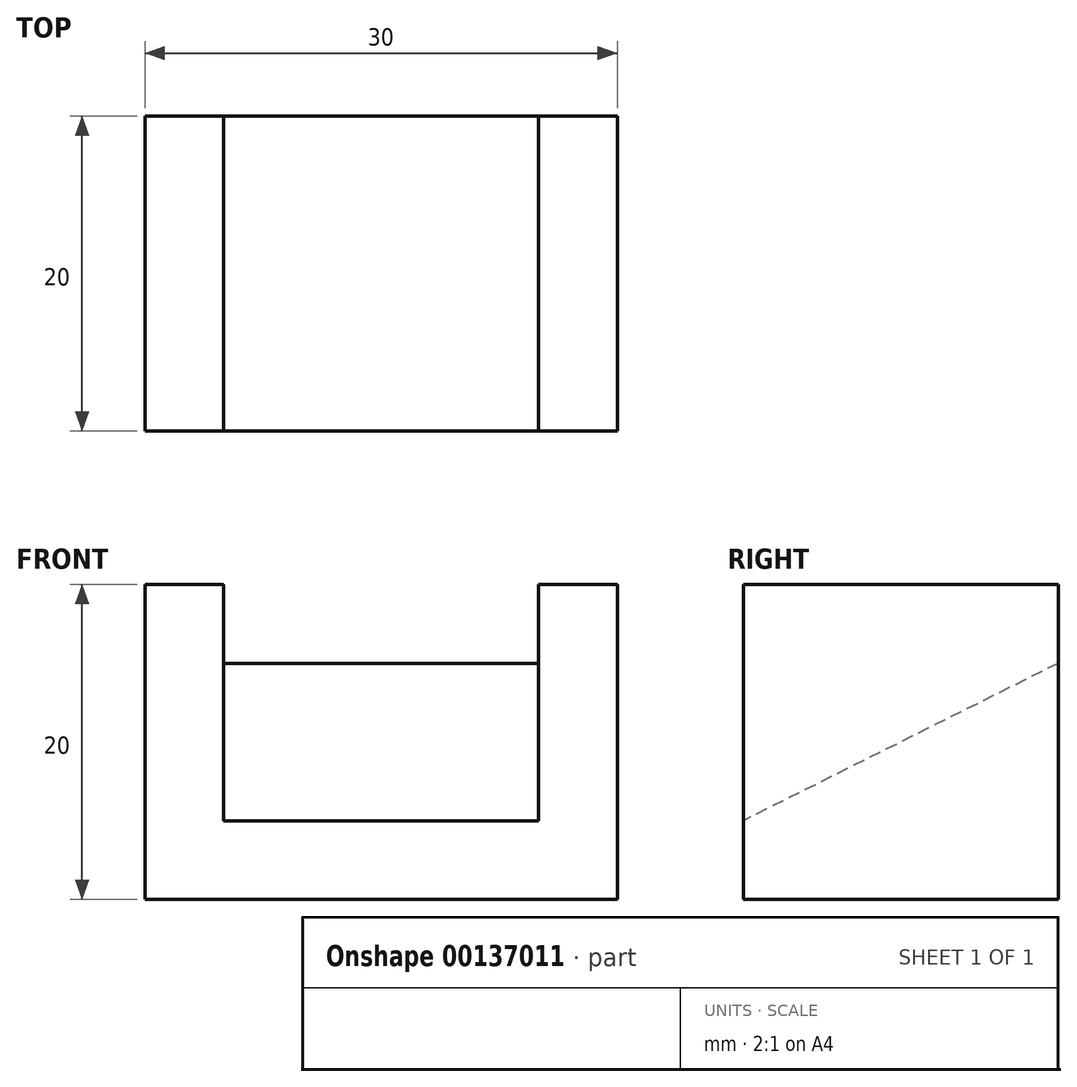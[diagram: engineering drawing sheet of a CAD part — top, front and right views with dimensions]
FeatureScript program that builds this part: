
annotation { "Feature Type Name" : "Feature", "Feature Type Description" : "" }
export const myFeature = defineFeature(function(context is Context, id is Id, definition is map)
    precondition{}
    {
        {
            var Q0;
            Q0=qCreatedBy(makeId("Front.planeOp"),FACE);
            var sketch = newSketch(context, id + "F0", { "sketchPlane" : qUnion([Q0])});
            skLineSegment(sketch, "E0", {"start": v(-10, 15) * mm, "end": v(-10, 0) * mm});
            skLineSegment(sketch, "E1", {"start": v(-10, 0) * mm, "end": v(10, 0) * mm});
            skLineSegment(sketch, "E2", {"start": v(10, 0) * mm, "end": v(10, 15) * mm});
            skLineSegment(sketch, "E3.0", {"start": v(15, -5) * mm, "end": v(15, 15) * mm});
            skLineSegment(sketch, "E3.1", {"start": v(-15, -5) * mm, "end": v(15, -5) * mm});
            skLineSegment(sketch, "E3.2", {"start": v(-15, 15) * mm, "end": v(-15, -5) * mm});
            skLineSegment(sketch, "E4", {"start": v(-15, 15) * mm, "end": v(-10, 15) * mm});
            skLineSegment(sketch, "E5", {"start": v(10, 15) * mm, "end": v(15, 15) * mm});
            skSolve(sketch);
        }
        {
            var Q0;
            Q0 = qSketchRegion(id + "F0", true);
            extrude(context, id + "F1", {"entities" : qUnion([Q0]), "depth" : 20 * mm});
        }
        {
            var Q0;
            Q0=makeQuery(id+"F1.opExtrude","SWEPT_FACE",FACE,{"disambiguationData":[OSD([sQuery(id+"F0.wireOp",EDGE,"E0")])]});
            var sketch = newSketch(context, id + "F2", { "sketchPlane" : qUnion([Q0])});
            skLineSegment(sketch, "E6", {"start": v(-20, 0) * mm, "end": v(0, 10) * mm});
            skLineSegment(sketch, "E7", {"start": v(-20, 0) * mm, "end": v(0, 0) * mm});
            skLineSegment(sketch, "E8", {"start": v(0, 0) * mm, "end": v(0, 10) * mm});
            skSolve(sketch);
        }
        {
            var Q0;
            Q0=makeQuery(id+"F2.imprint","IMPRINT",FACE,{"disambiguationData":[TD([[makeQuery(id+"F2.imprint","IMPRINT",EDGE,{"derivedFrom":sQuery(id+"F2.wireOp",EDGE,"E6")}),-1.0]])]});
            var Q1;
            Q1=makeQuery(id+"F1.opExtrude","SWEPT_FACE",FACE,{"disambiguationData":[OSD([sQuery(id+"F0.wireOp",EDGE,"E2")])]});
            extrude(context, id + "F3", {"entities" : qUnion([Q0]), "operationType" : NewBodyOperationType.ADD, "endBound" : BoundingType.UP_TO_SURFACE, "endBoundEntityFace" : qUnion([Q1]), "depth" : 25 * mm});
        }
    });
